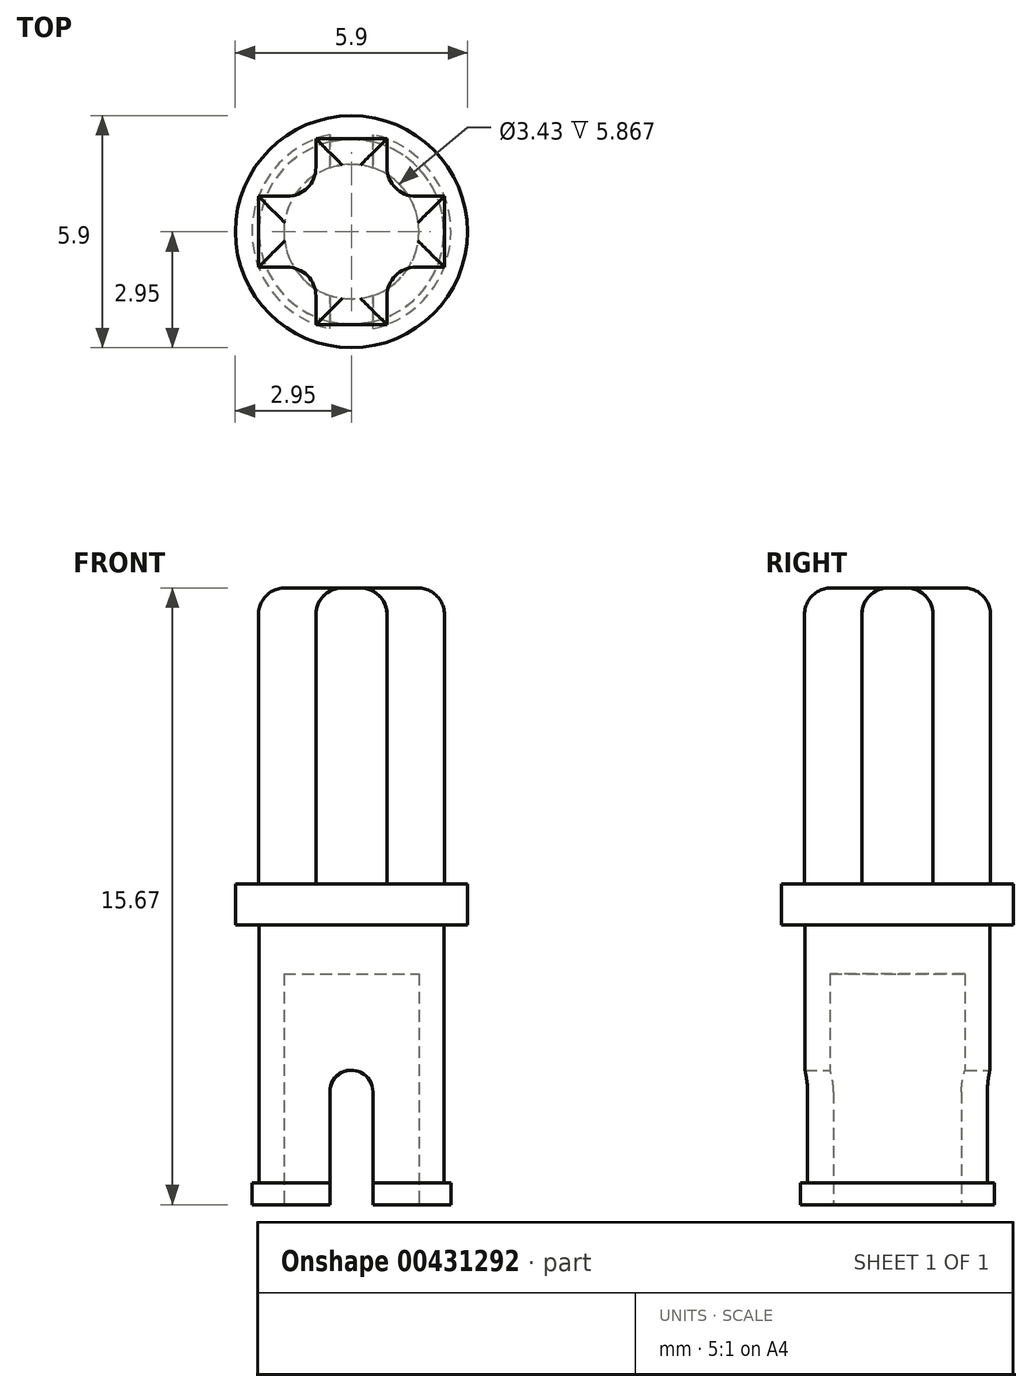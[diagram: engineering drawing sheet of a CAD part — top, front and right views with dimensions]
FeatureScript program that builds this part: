
annotation { "Feature Type Name" : "Feature", "Feature Type Description" : "" }
export const myFeature = defineFeature(function(context is Context, id is Id, definition is map)
    precondition{}
    {
        {
            var Q0;
            Q0=qCreatedBy(makeId("Top.planeOp"),FACE);
            var sketch = newSketch(context, id + "F0", { "sketchPlane" : qUnion([Q0])});
            skCircle(sketch, "E0", {"center": v(0, 0) * mm, "radius": 2.35 * mm});
            skSolve(sketch);
        }
        {
            var Q0;
            Q0 = qSketchRegion(id + "F0", true);
            extrude(context, id + "F1", {"entities" : qUnion([Q0]), "depth" : 15.67 * mm});
        }
        {
            var Q0;
            Q0=qCreatedBy(makeId("Front.planeOp"),FACE);
            var sketch = newSketch(context, id + "F2", { "sketchPlane" : qUnion([Q0])});
            skLineSegment(sketch, "E1.bottom", {"start": v(0.55, -2.87) * mm, "end": v(-0.55, -2.87) * mm});
            skLineSegment(sketch, "E1.top", {"start": v(0.55, 2.87) * mm, "end": v(-0.55, 2.87) * mm});
            skLineSegment(sketch, "E1.left", {"start": v(0.55, -2.87) * mm, "end": v(0.55, 2.87) * mm});
            skLineSegment(sketch, "E1.right", {"start": v(-0.55, -2.87) * mm, "end": v(-0.55, 2.87) * mm});
            skPoint(sketch, "E1.middle", {"position": v(0, 0) * mm});
            skCircle(sketch, "E2", {"center": v(0, 2.87) * mm, "radius": 0.55 * mm});
            skSolve(sketch);
        }
        {
            var Q0;
            Q0=makeQuery(id+"F1.opExtrude","CAP_FACE",FACE,{"disambiguationData":[OSD([sQuery(id+"F0.wireOp",EDGE,"E0")])],"isStart":true});
            var sketch = newSketch(context, id + "F3", { "sketchPlane" : qUnion([Q0])});
            skCircle(sketch, "E3", {"center": v(0, 0) * mm, "radius": 2.53 * mm});
            skSolve(sketch);
        }
        {
            var Q0;
            Q0 = qSketchRegion(id + "F3", true);
            extrude(context, id + "F4", {"entities" : qUnion([Q0]), "operationType" : NewBodyOperationType.ADD, "oppositeDirection" : true, "depth" : 0.56 * mm});
        }
        {
            var Q0;
            Q0 = qSketchRegion(id + "F2", true);
            extrude(context, id + "F5", {"entities" : qUnion([Q0]), "operationType" : NewBodyOperationType.REMOVE, "depth" : 25.4 * mm, "symmetric" : true});
        }
        {
            var Q0;
            Q0=makeQuery(id+"F1.opExtrude","CAP_FACE",FACE,{"disambiguationData":[OSD([sQuery(id+"F0.wireOp",EDGE,"E0")])],"isStart":false});
            var sketch = newSketch(context, id + "F6", { "sketchPlane" : qUnion([Q0])});
            skCircle(sketch, "E4", {"center": v(0, 0) * mm, "radius": 2.95 * mm});
            skSolve(sketch);
        }
        {
            var Q0;
            Q0 = qSketchRegion(id + "F6", true);
            extrude(context, id + "F7", {"entities" : qUnion([Q0]), "operationType" : NewBodyOperationType.ADD, "oppositeDirection" : true, "depth" : 8.56 * mm});
        }
        {
            var Q0;
            Q0=makeQuery(id+"F7.boolean.opBoolean","MERGE",FACE,{"derivedFrom":[makeQuery(id+"F1.opExtrude","CAP_FACE",FACE,{"disambiguationData":[OSD([sQuery(id+"F0.wireOp",EDGE,"E0")])],"isStart":false}),makeQuery(id+"F7.opExtrude","CAP_FACE",FACE,{"disambiguationData":[OSD([sQuery(id+"F6.wireOp",EDGE,"E4")])],"isStart":true})]});
            var sketch = newSketch(context, id + "F8", { "sketchPlane" : qUnion([Q0])});
            skCircle(sketch, "E5", {"center": v(0, 0) * mm, "radius": 12.7 * mm});
            skSolve(sketch);
        }
        {
            var Q0;
            Q0 = qSketchRegion(id + "F8", true);
            extrude(context, id + "F9", {"entities" : qUnion([Q0]), "operationType" : NewBodyOperationType.REMOVE, "oppositeDirection" : true, "depth" : 7.52 * mm});
        }
        {
            var Q0;
            Q0=makeQuery(id+"F9.boolean.opBoolean","COPY",FACE,{"derivedFrom":makeQuery(id+"F9.opExtrude","CAP_FACE",FACE,{"disambiguationData":[OSD([sQuery(id+"F8.wireOp",EDGE,"E5")])],"isStart":false})});
            var sketch = newSketch(context, id + "F10", { "sketchPlane" : qUnion([Q0])});
            skLineSegment(sketch, "E6.bottom", {"start": v(2.36, -0.9) * mm, "end": v(-2.36, -0.9) * mm});
            skLineSegment(sketch, "E6.top", {"start": v(2.36, 0.9) * mm, "end": v(-2.36, 0.9) * mm});
            skLineSegment(sketch, "E6.left", {"start": v(2.36, -0.9) * mm, "end": v(2.36, 0.9) * mm});
            skLineSegment(sketch, "E6.right", {"start": v(-2.36, -0.9) * mm, "end": v(-2.36, 0.9) * mm});
            skPoint(sketch, "E6.middle", {"position": v(0, 0) * mm});
            skLineSegment(sketch, "E7.bottom", {"start": v(-0.9, -2.36) * mm, "end": v(0.9, -2.36) * mm});
            skLineSegment(sketch, "E7.top", {"start": v(-0.9, 2.36) * mm, "end": v(0.9, 2.36) * mm});
            skLineSegment(sketch, "E7.left", {"start": v(-0.9, -2.36) * mm, "end": v(-0.9, 2.36) * mm});
            skLineSegment(sketch, "E7.right", {"start": v(0.9, -2.36) * mm, "end": v(0.9, 2.36) * mm});
            skSolve(sketch);
        }
        {
            var Q0;
            Q0 = qSketchRegion(id + "F10", true);
            extrude(context, id + "F11", {"entities" : qUnion([Q0]), "operationType" : NewBodyOperationType.ADD, "depth" : 7.52 * mm});
        }
        {
            var Q0;
            Q0=makeQuery(id+"F11.opExtrude","SWEPT_EDGE",EDGE,{"disambiguationData":[OSD([sQuery(id+"F10.wireOp",EDGE,"E6.bottom"),sQuery(id+"F10.wireOp",EDGE,"E7.left")])]});
            var Q1;
            Q1=makeQuery(id+"F11.opExtrude","SWEPT_EDGE",EDGE,{"disambiguationData":[OSD([sQuery(id+"F10.wireOp",EDGE,"E6.top"),sQuery(id+"F10.wireOp",EDGE,"E7.right")])]});
            var Q2;
            Q2=makeQuery(id+"F11.opExtrude","SWEPT_EDGE",EDGE,{"disambiguationData":[OSD([sQuery(id+"F10.wireOp",EDGE,"E6.bottom"),sQuery(id+"F10.wireOp",EDGE,"E7.right")])]});
            var Q3;
            Q3=makeQuery(id+"F11.opExtrude","SWEPT_EDGE",EDGE,{"disambiguationData":[OSD([sQuery(id+"F10.wireOp",EDGE,"E6.top"),sQuery(id+"F10.wireOp",EDGE,"E7.left")])]});
            fillet(context, id + "F12", {"entities" : qUnion([Q0, Q1, Q2, Q3]), "radius" : 0.74 * mm, "tangentPropagation" : true, "allowEdgeOverflow" : false});
        }
        {
            var Q0;
            Q0=makeQuery(id+"F11.opExtrude","CAP_FACE",FACE,{"disambiguationData":[OSD([sQuery(id+"F10.wireOp",EDGE,"E6.bottom"),sQuery(id+"F10.wireOp",EDGE,"E6.top"),sQuery(id+"F10.wireOp",EDGE,"E6.left"),sQuery(id+"F10.wireOp",EDGE,"E6.right"),sQuery(id+"F10.wireOp",EDGE,"E7.bottom"),sQuery(id+"F10.wireOp",EDGE,"E7.top"),sQuery(id+"F10.wireOp",EDGE,"E7.left"),sQuery(id+"F10.wireOp",EDGE,"E7.right")])],"isStart":false});
            fillet(context, id + "F13", {"entities" : qUnion([Q0]), "radius" : 0.67 * mm, "tangentPropagation" : true, "allowEdgeOverflow" : false});
        }
        {
            var Q0;
            {var subQ0=sQuery(id+"F3.wireOp",EDGE,"E3");Q0=makeQuery(id+"F5.boolean.opBoolean","SPLIT",FACE,{"disambiguationData":[TD([makeQuery(id+"F5.opExtrude","SWEPT_FACE",FACE,{"disambiguationData":[OSD([sQuery(id+"F2.wireOp",EDGE,"E1.left")])]})])],"derivedFrom":makeQuery(id+"F4.boolean.opBoolean","MERGE",FACE,{"derivedFrom":[makeQuery(id+"F1.opExtrude","CAP_FACE",FACE,{"disambiguationData":[OSD([sQuery(id+"F0.wireOp",EDGE,"E0")])],"isStart":true}),makeQuery(id+"F4.opExtrude","CAP_FACE",FACE,{"disambiguationData":[OSD([subQ0])],"isStart":true})]})});}
            var sketch = newSketch(context, id + "F14", { "sketchPlane" : qUnion([Q0])});
            skCircle(sketch, "E8", {"center": v(0, 0) * mm, "radius": 1.71 * mm});
            skSolve(sketch);
        }
        {
            var Q0;
            Q0 = qSketchRegion(id + "F14", true);
            extrude(context, id + "F15", {"entities" : qUnion([Q0]), "operationType" : NewBodyOperationType.REMOVE, "oppositeDirection" : true, "depth" : 5.87 * mm});
        }
    });
